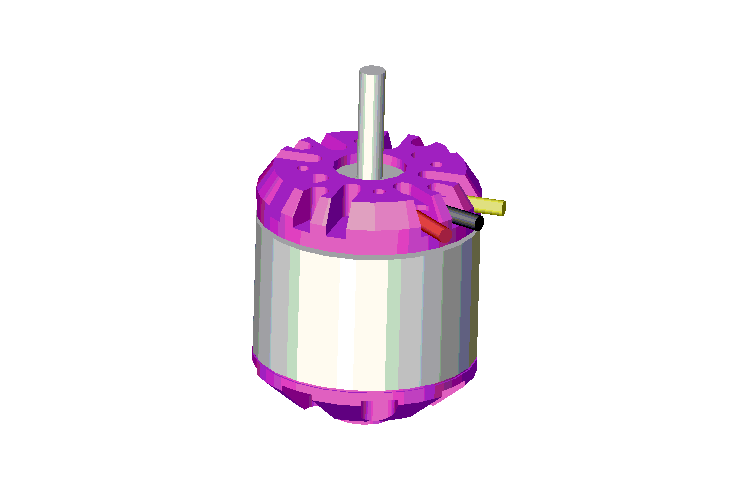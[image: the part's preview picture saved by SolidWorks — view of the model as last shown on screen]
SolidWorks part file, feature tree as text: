
SOLIDWORKS PART (.sldprt)
format: sldprt  version: not decoded by parser v0  size: 581,632 bytes
history: native  units: mm
features: sketch x14, extrude x10, plane x8, cut_extrude x4, pattern_circular x3, chamfer x2 (+8 scaffold rows collapsed)
feature tree (49):
  scaffold x8  (default folders/planes/origin — collapsed)
  sketch  "Sketch1"  dims[D1=5.0mm]
  extrude  "Base-Extrude"  Depth=70mm
  plane  "Plane1"  Offset=19.5mm
  sketch  "Sketch2"  dims[D1=42.5mm]
  extrude  "Boss-Extrude1"  Depth=9.5mm
  chamfer  "Chamfer1"  Distance=4.5mm
  sketch  "Sketch3"  dims[D1=14.0mm D2=5.0mm]
  cut_extrude  "Cut-Extrude2"  Depth=2mm
  sketch  "Sketch4"  dims[c1.D1=25.4mm c1.D2=2.5mm c1.D3=2.5mm c1.D4=2.5mm c1.D5=2.5mm c2.D1=12.7mm c2.D6=12.7mm c2.D7=12.7mm c2.D8=12.7mm]
  cut_extrude  "Cut-Extrude3"  Depth=5mm
  plane  "Plane2"  Offset=1mm
  sketch  "Sketch6"
  extrude  "Boss-Extrude2"  Depth=26.5mm
  plane  "Plane3"  Offset=46mm
  sketch  "Sketch8"
  extrude  "Boss-Extrude5"  Depth=0.5mm
  sketch  "Sketch9"
  extrude  "Boss-Extrude6"  [1 undecoded]
  chamfer  "Chamfer2"  Distance=7mm Angle=40deg
  plane  "Plane4"  Offset=0.5mm
  sketch  "Sketch11"  dims[D1=11.87mm]
  extrude  "Boss-Extrude7"  [1 undecoded]
  sketch  "Sketch12"  dims[c1.D4=2.0mm c1.D5=~26.887296mm c1.D9=~24.031358mm c1.D8=2.0mm c1.D12=~23.183644mm c1.D1=~25.572683mm c2.D1=25.0deg c2.D2=~29.490335mm c3.D2=45.0deg c3.D3=~25.572683mm c4.D3=~108.929932deg c5.D3=~25.572683mm c6.D3=65.0deg c6.D4=2.0mm c6.D5=2.0mm c6.D6=16.0mm c6.D2=~11.313708mm c6.D7=~25.572683mm c7.D7=45.0deg c7.D8=2.0mm c7.D9=2.0mm c7.D10=11.5mm c8.D8=4.0mm c8.D11=~10.812808mm c9.D11=20.0deg c10.D11=~12.447989mm c10.D3=~12.447989mm c11.D3=20.0deg c11.D7=~12.447989mm c12.D7=40.0deg c12.D12=2.0mm c12.D13=2.0mm c12.D14=11.5mm c13.D7=~12.447989mm c14.D7=40.0deg c14.D13=~11.597215mm c14.D15=4.0mm]
  cut_extrude  "Cut-Extrude4"  Depth=6.5mm
  pattern_circular  "CirPattern1"  Count=4 Angle=360deg
  plane  "Plane5"
  sketch  "Sketch13"  dims[D1=3.0mm D2=1.75mm]
  extrude  "Boss-Extrude8"  Depth=15mm
  plane  "Plane6"
  sketch  "Sketch14"  dims[D1=3.0mm D2=1.785mm]
  extrude  "Boss-Extrude9"  Depth=10mm
  plane  "Plane7"
  sketch  "Sketch15"  dims[D1=3.0mm D2=1.75mm]
  extrude  "Boss-Extrude10"  Depth=15mm
  plane  "Plane8"  Offset=2.35mm
  sketch  "Sketch16"  dims[D1=5.0mm D2=6.25mm D3=~6.118235mm D4=~4.996525mm]
  extrude  "Boss-Extrude11"  Depth=1mm
  pattern_circular  "CirPattern2"  Count=3 Angle=40deg
  sketch  "Sketch17"  dims[c1.D5=7.0mm c1.D3=7.0mm c1.D9=3.0mm c1.D1=~22.571116mm c2.D1=45.0deg c2.D2=3.5mm c2.D3=3.5mm c2.D4=12.5mm c3.D1=10.0mm c3.D2=10.0mm c3.D6=~18.384776mm c3.D4=12.5mm c4.D6=18.0mm c4.D7=5.0mm c4.D8=9.5mm]
  cut_extrude  "Cut-Extrude5"  Depth=7mm
  pattern_circular  "CirPattern3"  Count=4 Angle=360deg
decode coverage: 28 of 33 modeling features carry decoded parameters
note: ~ marks probable driven/reference dimensions
note: 2 parameter values undecoded
note: suppression state not decoded; provenance and decode notes live in map.json
